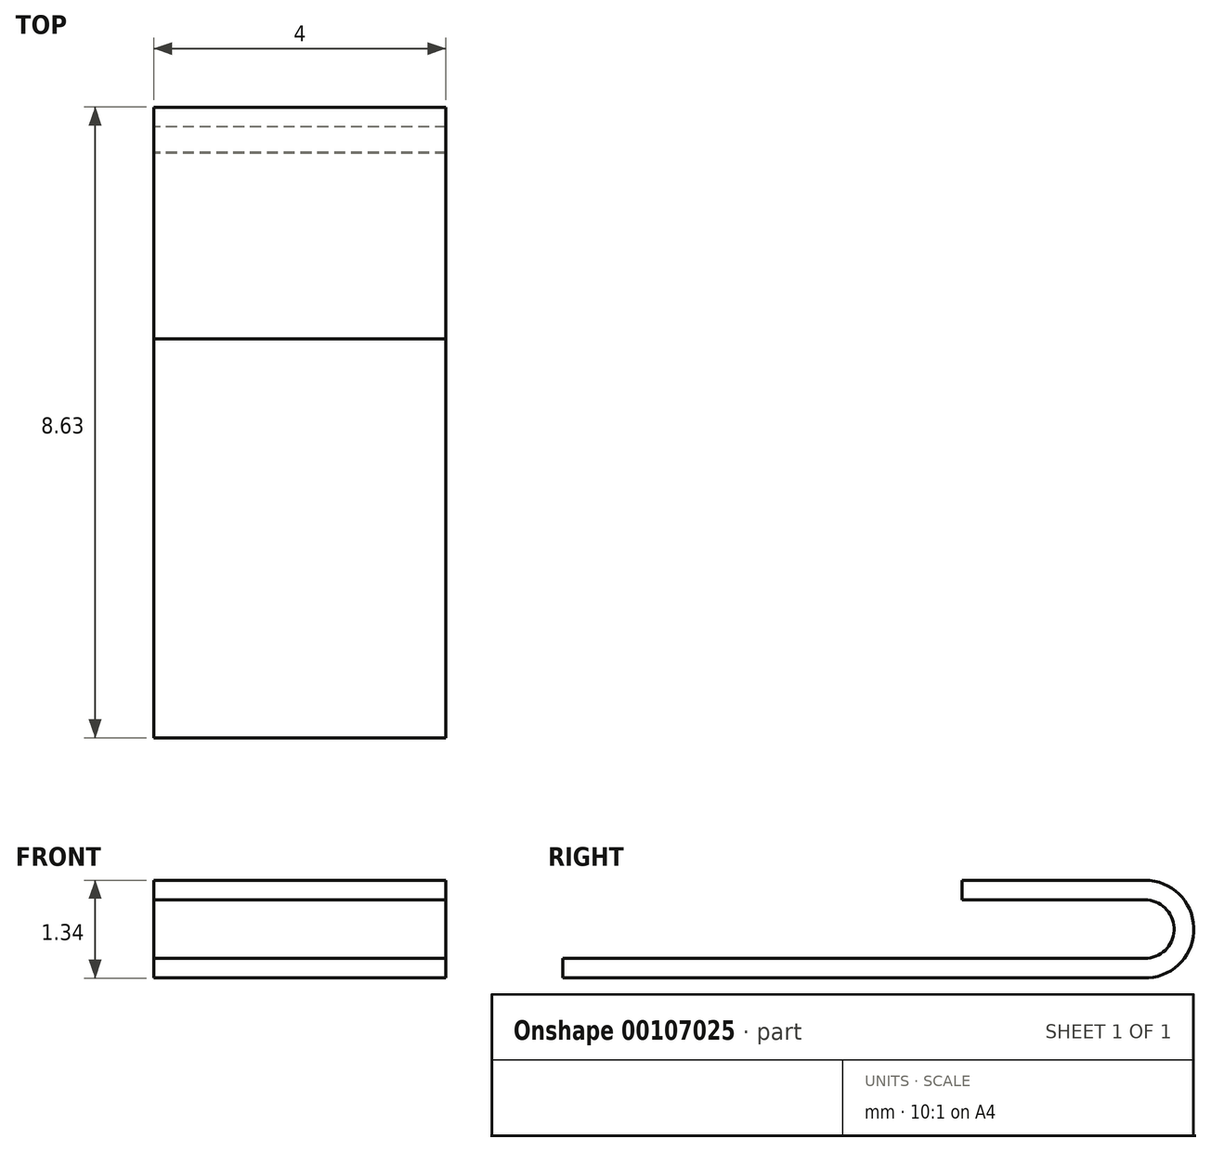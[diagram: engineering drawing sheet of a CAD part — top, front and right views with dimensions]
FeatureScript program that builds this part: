
annotation { "Feature Type Name" : "Feature", "Feature Type Description" : "" }
export const myFeature = defineFeature(function(context is Context, id is Id, definition is map)
    precondition{}
    {
        {
            var Q0;
            Q0=qCreatedBy(makeId("Right.planeOp"),FACE);
            var sketch = newSketch(context, id + "F0", { "sketchPlane" : qUnion([Q0])});
            skLineSegment(sketch, "E0", {"start": v(0, 0) * mm, "end": v(2.5, 0) * mm});
            skArc(sketch, "E1", {"start": v(2.5, 0) * mm, "mid": v(2.9, -0.38) * mm, "end": v(2.54, -0.8) * mm});
            skLineSegment(sketch, "E2", {"start": v(2.54, -0.8) * mm, "end": v(-5.46, -0.8) * mm});
            skLineSegment(sketch, "E3.0", {"start": v(2.55, -1.07) * mm, "end": v(-5.46, -1.07) * mm});
            skArc(sketch, "E3.1", {"start": v(2.5, 0.27) * mm, "mid": v(3.17, -0.38) * mm, "end": v(2.55, -1.07) * mm});
            skLineSegment(sketch, "E3.2", {"start": v(0, 0.27) * mm, "end": v(2.5, 0.27) * mm});
            skLineSegment(sketch, "E4", {"start": v(0, 0) * mm, "end": v(0, 0.27) * mm});
            skLineSegment(sketch, "E5", {"start": v(-5.46, -0.8) * mm, "end": v(-5.46, -1.07) * mm});
            skSolve(sketch);
        }
        {
            var Q0;
            Q0 = qSketchRegion(id + "F0", true);
            extrude(context, id + "F1", {"entities" : qUnion([Q0]), "depth" : 4 * mm});
        }
    });
